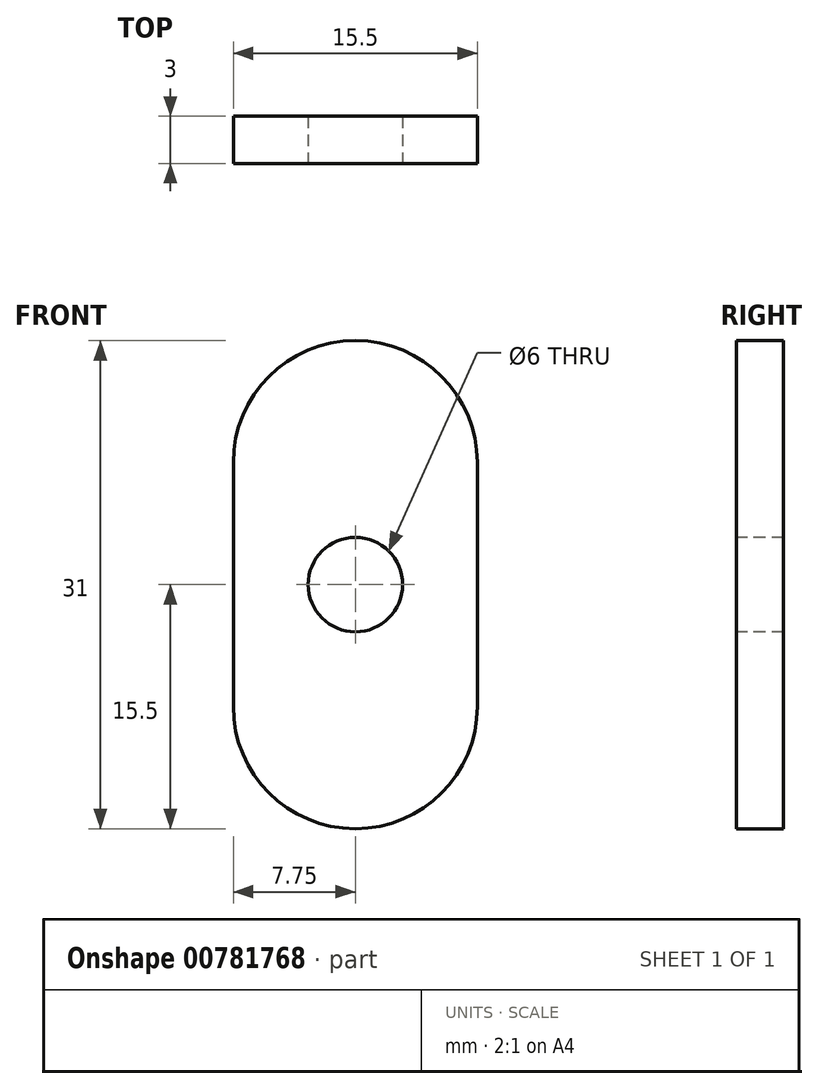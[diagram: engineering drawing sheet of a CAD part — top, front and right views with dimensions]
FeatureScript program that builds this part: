
annotation { "Feature Type Name" : "Feature", "Feature Type Description" : "" }
export const myFeature = defineFeature(function(context is Context, id is Id, definition is map)
    precondition{}
    {
        {
            var Q0;
            Q0=qCreatedBy(makeId("Front.planeOp"),FACE);
            var sketch = newSketch(context, id + "F0", { "sketchPlane" : qUnion([Q0])});
            skLineSegment(sketch, "E0.bottom", {"start": v(0, 15.5) * mm, "end": v(0, 15.5) * mm});
            skLineSegment(sketch, "E0.top", {"start": v(0, -15.5) * mm, "end": v(0, -15.5) * mm});
            skLineSegment(sketch, "E0.left", {"start": v(-7.75, 7.75) * mm, "end": v(-7.75, -7.75) * mm});
            skLineSegment(sketch, "E0.right", {"start": v(7.75, 7.75) * mm, "end": v(7.75, -7.75) * mm});
            skPoint(sketch, "E0.middle", {"position": v(0, 0) * mm});
            skPoint(sketch, "E1.visualSharp", {"position": v(-7.75, 15.5) * mm});
            skArc(sketch, "E1.filletArc", {"start": v(0, 15.5) * mm, "mid": v(-5.48, 13.23) * mm, "end": v(-7.75, 7.75) * mm});
            skPoint(sketch, "E2.visualSharp", {"position": v(7.75, 15.5) * mm});
            skArc(sketch, "E2.filletArc", {"start": v(7.75, 7.75) * mm, "mid": v(5.48, 13.23) * mm, "end": v(0, 15.5) * mm});
            skPoint(sketch, "E3.visualSharp", {"position": v(7.75, -15.5) * mm});
            skArc(sketch, "E3.filletArc", {"start": v(0, -15.5) * mm, "mid": v(5.48, -13.23) * mm, "end": v(7.75, -7.75) * mm});
            skPoint(sketch, "E4.visualSharp", {"position": v(-7.75, -15.5) * mm});
            skArc(sketch, "E4.filletArc", {"start": v(-7.75, -7.75) * mm, "mid": v(-5.48, -13.23) * mm, "end": v(0, -15.5) * mm});
            skSolve(sketch);
        }
        {
            var Q0;
            Q0=makeQuery(id+"F0.imprint","IMPRINT",FACE,{"disambiguationData":[TD([[makeQuery(id+"F0.imprint","IMPRINT",EDGE,{"derivedFrom":sQuery(id+"F0.wireOp",EDGE,"E0.left")}),1.0]])]});
            extrude(context, id + "F1", {"entities" : qUnion([Q0]), "depth" : 3 * mm, "offsetDistance" : 25 * mm});
        }
        {
            var Q0;
            Q0=makeQuery(id+"F1.opExtrude","CAP_FACE",FACE,{"disambiguationData":[OSD([sQuery(id+"F0.wireOp",EDGE,"E0.bottom"),sQuery(id+"F0.wireOp",EDGE,"E0.top"),sQuery(id+"F0.wireOp",EDGE,"E0.left"),sQuery(id+"F0.wireOp",EDGE,"E0.right"),sQuery(id+"F0.wireOp",EDGE,"E1.filletArc"),sQuery(id+"F0.wireOp",EDGE,"E2.filletArc"),sQuery(id+"F0.wireOp",EDGE,"E3.filletArc"),sQuery(id+"F0.wireOp",EDGE,"E4.filletArc")])],"isStart":false});
            var sketch = newSketch(context, id + "F2", { "sketchPlane" : qUnion([Q0])});
            skCircle(sketch, "E5", {"center": v(0, 0) * mm, "radius": 3 * mm});
            skSolve(sketch);
        }
        {
            var Q0;
            Q0=makeQuery(id+"F2.imprint","IMPRINT",FACE,{"disambiguationData":[TD([[makeQuery(id+"F2.imprint","IMPRINT",EDGE,{"derivedFrom":sQuery(id+"F2.wireOp",EDGE,"E5")}),1.0]])]});
            extrude(context, id + "F3", {"entities" : qUnion([Q0]), "operationType" : NewBodyOperationType.REMOVE, "oppositeDirection" : true, "depth" : 25 * mm, "offsetDistance" : 25 * mm});
        }
    });
